# Revit family: FA_ПеремычкаГибкая_ПГС300_41915_EZETEK
name_source: partatom
category: Системы пожарной сигнализации
revit_build: Autodesk Revit 2017 (Build: 20170118_1100(x64)
units: mm (PartAtom-declared; Revit-internal decimal feet)

## family parameters
Всегда вертикально = Да
На основе рабочей плоскости = Нет
Общий = Нет
При загрузке вырезать с полостями = Нет
Размер круглого соединителя = Использовать радиус
Сохранять ориентацию аннотаций = Нет
Тип детали = Нормальный
Точка расчета площади = Нет

## types (1)
- ПеремычкаГибкая_ПГС300_41915
    ADSK_Версия Revit = 2017
    ADSK_Единица измерения = шт.
    ADSK_Завод-изготовитель = Ezetek
    ADSK_Код изделия = 41915
    ADSK_Количество = 1
    ADSK_Марка = 41915
    ADSK_Масса = 0.16
    ADSK_Масса_Текст = 0.16
    ADSK_Материал = BIMLIB_Сталь_Оцинкованная_EZETEK
    ADSK_Наименование = Перемычка гибкая ПГС 300, оцинк.
    ADSK_Обозначение = 41915
    URL = https://ezetek.ru
    Группа модели = FA_ПеремычкаГибкая_ПГС300_41915_EZETEK
    Изготовитель = Ezetek
    Описание = Перемычка ПГС используется для заземления между трубопроводами и другими протяжёнными металлическими предметами (каркас сооружения, оболочки кабелей, металлические конструкции и т.д.) в местах их взаимного сближения на расстоянии 10 см и меньше через каждые 20 м длинны следует присоединять перемычки, для того чтобы не допускать образования незамкнутых контуров. В местах соединений необходимо устройство перемычек диаметром не менее 5 мм.
